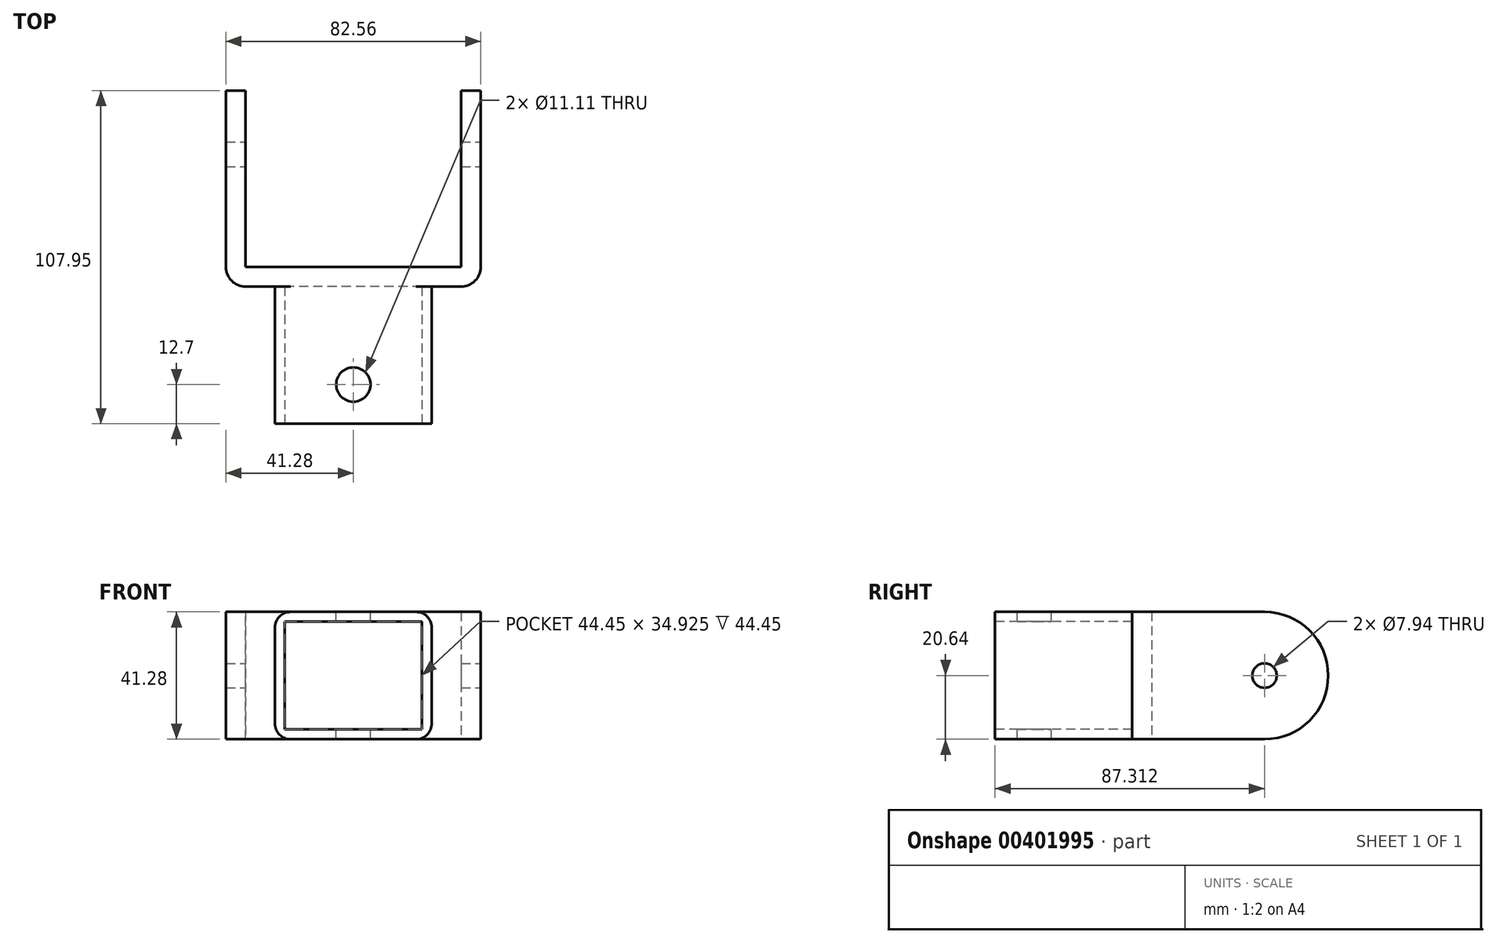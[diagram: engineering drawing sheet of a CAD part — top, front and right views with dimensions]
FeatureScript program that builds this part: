
annotation { "Feature Type Name" : "Feature", "Feature Type Description" : "" }
export const myFeature = defineFeature(function(context is Context, id is Id, definition is map)
    precondition{}
    {
        {
            var Q0;
            Q0=qCreatedBy(makeId("Front.planeOp"),FACE);
            var sketch = newSketch(context, id + "F0", { "sketchPlane" : qUnion([Q0])});
            skLineSegment(sketch, "E0.bottom", {"start": v(25.4, 20.64) * mm, "end": v(-25.4, 20.64) * mm});
            skLineSegment(sketch, "E0.top", {"start": v(25.4, -20.64) * mm, "end": v(-25.4, -20.64) * mm});
            skLineSegment(sketch, "E0.left", {"start": v(25.4, 20.64) * mm, "end": v(25.4, -20.64) * mm});
            skLineSegment(sketch, "E0.right", {"start": v(-25.4, 20.64) * mm, "end": v(-25.4, -20.64) * mm});
            skPoint(sketch, "E0.middle", {"position": v(0, 0) * mm});
            skLineSegment(sketch, "E1.bottom", {"start": v(22.23, 17.46) * mm, "end": v(-22.23, 17.46) * mm});
            skLineSegment(sketch, "E1.top", {"start": v(22.23, -17.46) * mm, "end": v(-22.23, -17.46) * mm});
            skLineSegment(sketch, "E1.left", {"start": v(22.23, 17.46) * mm, "end": v(22.23, -17.46) * mm});
            skLineSegment(sketch, "E1.right", {"start": v(-22.23, 17.46) * mm, "end": v(-22.23, -17.46) * mm});
            skSolve(sketch);
        }
        {
            var Q0;
            Q0=makeQuery(id+"F0.imprint","IMPRINT",FACE,{"disambiguationData":[TD([[makeQuery(id+"F0.imprint","IMPRINT",EDGE,{"derivedFrom":sQuery(id+"F0.wireOp",EDGE,"E0.bottom")}),1.0]])]});
            extrude(context, id + "F1", {"entities" : qUnion([Q0]), "oppositeDirection" : true, "depth" : 44.45 * mm});
        }
        {
            var Q0;
            Q0=qCreatedBy(makeId("Top.planeOp"),FACE);
            var sketch = newSketch(context, id + "F2", { "sketchPlane" : qUnion([Q0])});
            skLineSegment(sketch, "E2.bottom", {"start": v(41.27, 107.95) * mm, "end": v(34.93, 107.95) * mm});
            skLineSegment(sketch, "E2.top", {"start": v(41.28, 44.45) * mm, "end": v(-41.28, 44.45) * mm});
            skLineSegment(sketch, "E2.left", {"start": v(41.27, 107.95) * mm, "end": v(41.28, 44.45) * mm});
            skLineSegment(sketch, "E2.right", {"start": v(-41.28, 107.95) * mm, "end": v(-41.27, 44.45) * mm});
            skPoint(sketch, "E2.middle", {"position": v(0, 76.2) * mm});
            skLineSegment(sketch, "E3.top", {"start": v(34.93, 50.8) * mm, "end": v(-34.93, 50.8) * mm});
            skLineSegment(sketch, "E3.left", {"start": v(34.93, 101.6) * mm, "end": v(34.93, 50.8) * mm});
            skLineSegment(sketch, "E3.right", {"start": v(-34.93, 101.6) * mm, "end": v(-34.93, 50.8) * mm});
            skLineSegment(sketch, "E4", {"start": v(-34.93, 101.6) * mm, "end": v(-34.93, 107.95) * mm});
            skLineSegment(sketch, "E5", {"start": v(34.93, 101.6) * mm, "end": v(34.93, 107.95) * mm});
            skLineSegment(sketch, "E6.trimOffspring", {"start": v(-34.93, 107.95) * mm, "end": v(-41.28, 107.95) * mm});
            skSolve(sketch);
        }
        {
            var Q0;
            Q0 = qSketchRegion(id + "F2", true);
            extrude(context, id + "F3", {"entities" : qUnion([Q0]), "operationType" : NewBodyOperationType.ADD, "depth" : 41.27 * mm, "symmetric" : true});
        }
        {
            var Q0;
            Q0=makeQuery(id+"F3.opExtrude","SWEPT_FACE",FACE,{"disambiguationData":[OSD([sQuery(id+"F2.wireOp",EDGE,"E2.right")])]});
            var sketch = newSketch(context, id + "F4", { "sketchPlane" : qUnion([Q0])});
            skPoint(sketch, "E7", {"position": v(-87.31, 0) * mm});
            skCircle(sketch, "E8", {"center": v(-87.31, 0) * mm, "radius": 20.64 * mm});
            skSolve(sketch);
        }
        {
            var Q0;
            {var subQ0=sQuery(id+"F4.wireOp",EDGE,"E8");var subQ1=sQuery(id+"F2.wireOp",EDGE,"E2.right");var subQ4=makeQuery(id+"F3.opExtrude","CAP_EDGE",EDGE,{"disambiguationData":[OSD([subQ1])],"isStart":true});var subQ5=makeQuery(id+"F4.imprint","INTERSECT",VERTEX,{"derivedFrom":[subQ4,subQ0]});Q0=makeQuery(id+"F4.imprint","IMPRINT",FACE,{"disambiguationData":[TD([[makeQuery(id+"F4.imprint","IMPRINT",EDGE,{"disambiguationData":[TD([[subQ5,1.0]])],"derivedFrom":subQ0}),-1.0]])]});}
            var Q1;
            {var subQ0=sQuery(id+"F4.wireOp",EDGE,"E8");var subQ1=sQuery(id+"F2.wireOp",EDGE,"E2.right");var subQ4=makeQuery(id+"F3.opExtrude","CAP_EDGE",EDGE,{"disambiguationData":[OSD([subQ1])],"isStart":false});var subQ5=makeQuery(id+"F4.imprint","INTERSECT",VERTEX,{"derivedFrom":[subQ4,subQ0]});Q1=makeQuery(id+"F4.imprint","IMPRINT",FACE,{"disambiguationData":[TD([[makeQuery(id+"F4.imprint","IMPRINT",EDGE,{"disambiguationData":[TD([[subQ5,-1.0]])],"derivedFrom":subQ0}),-1.0]])]});}
            extrude(context, id + "F5", {"entities" : qUnion([Q0, Q1]), "operationType" : NewBodyOperationType.REMOVE, "endBound" : BoundingType.THROUGH_ALL, "oppositeDirection" : true, "depth" : 25.4 * mm});
        }
        {
            var Q0;
            Q0=makeQuery(id+"F3.opExtrude","SWEPT_FACE",FACE,{"disambiguationData":[OSD([sQuery(id+"F2.wireOp",EDGE,"E2.right")])]});
            var sketch = newSketch(context, id + "F6", { "sketchPlane" : qUnion([Q0])});
            skPoint(sketch, "E9", {"position": v(-87.31, 0) * mm});
            skSolve(sketch);
        }
        {
            var Q0;
            Q0=sQuery(id+"F6.wireOp",VERTEX,"E9");
            var Q1;
            Q1=makeQuery(id+"F1.opExtrude","SWEPT_BODY",BODY,{"disambiguationData":[OSD([sQuery(id+"F0.wireOp",EDGE,"E0.bottom"),sQuery(id+"F0.wireOp",EDGE,"E0.top"),sQuery(id+"F0.wireOp",EDGE,"E0.left"),sQuery(id+"F0.wireOp",EDGE,"E0.right"),sQuery(id+"F0.wireOp",EDGE,"E1.bottom"),sQuery(id+"F0.wireOp",EDGE,"E1.top"),sQuery(id+"F0.wireOp",EDGE,"E1.left"),sQuery(id+"F0.wireOp",EDGE,"E1.right")])]});
            hole(context, id + "F7", {"style" : HoleStyle.SIMPLE, "endStyle" : HoleEndStyle.THROUGH, "holeDiameter" : 7.94 * mm, "isTappedThrough" : true, "tappedDepth" : 12.7 * mm, "tapClearance" : 3, "locations" : qUnion([Q0]), "scope" : qUnion([Q1])});
        }
        {
            var Q0;
            Q0=makeQuery(id+"F3.opExtrude","SWEPT_EDGE",EDGE,{"disambiguationData":[OSD([sQuery(id+"F2.wireOp",EDGE,"E2.top"),sQuery(id+"F2.wireOp",EDGE,"E2.right")])]});
            var Q1;
            Q1=makeQuery(id+"F3.opExtrude","SWEPT_EDGE",EDGE,{"disambiguationData":[OSD([sQuery(id+"F2.wireOp",EDGE,"E2.top"),sQuery(id+"F2.wireOp",EDGE,"E2.left")])]});
            fillet(context, id + "F8", {"entities" : qUnion([Q0, Q1]), "radius" : 6.35 * mm, "tangentPropagation" : true, "allowEdgeOverflow" : false});
        }
        {
            var Q0;
            Q0=makeQuery(id+"F1.opExtrude","SWEPT_EDGE",EDGE,{"disambiguationData":[OSD([sQuery(id+"F0.wireOp",EDGE,"E0.bottom"),sQuery(id+"F0.wireOp",EDGE,"E0.right")])]});
            var Q1;
            Q1=makeQuery(id+"F1.opExtrude","SWEPT_EDGE",EDGE,{"disambiguationData":[OSD([sQuery(id+"F0.wireOp",EDGE,"E0.bottom"),sQuery(id+"F0.wireOp",EDGE,"E0.left")])]});
            var Q2;
            Q2=makeQuery(id+"F1.opExtrude","SWEPT_EDGE",EDGE,{"disambiguationData":[OSD([sQuery(id+"F0.wireOp",EDGE,"E0.top"),sQuery(id+"F0.wireOp",EDGE,"E0.left")])]});
            var Q3;
            Q3=makeQuery(id+"F1.opExtrude","SWEPT_EDGE",EDGE,{"disambiguationData":[OSD([sQuery(id+"F0.wireOp",EDGE,"E0.top"),sQuery(id+"F0.wireOp",EDGE,"E0.right")])]});
            fillet(context, id + "F9", {"entities" : qUnion([Q0, Q1, Q2, Q3]), "radius" : 5.08 * mm, "tangentPropagation" : true, "allowEdgeOverflow" : false});
        }
        {
            var Q0;
            Q0=makeQuery(id+"F3.boolean.opBoolean","MERGE",FACE,{"derivedFrom":[makeQuery(id+"F1.opExtrude","SWEPT_FACE",FACE,{"disambiguationData":[OSD([sQuery(id+"F0.wireOp",EDGE,"E0.top")])]}),makeQuery(id+"F3.opExtrude","CAP_FACE",FACE,{"disambiguationData":[OSD([sQuery(id+"F2.wireOp",EDGE,"E2.bottom"),sQuery(id+"F2.wireOp",EDGE,"E2.top"),sQuery(id+"F2.wireOp",EDGE,"E2.left"),sQuery(id+"F2.wireOp",EDGE,"E2.right"),sQuery(id+"F2.wireOp",EDGE,"E3.top"),sQuery(id+"F2.wireOp",EDGE,"E3.left"),sQuery(id+"F2.wireOp",EDGE,"E3.right"),sQuery(id+"F2.wireOp",EDGE,"E4"),sQuery(id+"F2.wireOp",EDGE,"E5"),sQuery(id+"F2.wireOp",EDGE,"E6.trimOffspring")])],"isStart":true})]});
            var sketch = newSketch(context, id + "F10", { "sketchPlane" : qUnion([Q0])});
            skPoint(sketch, "E10", {"position": v(0, -12.7) * mm});
            skSolve(sketch);
        }
        {
            var Q0;
            Q0=sQuery(id+"F10.wireOp",VERTEX,"E10");
            var Q1;
            Q1=makeQuery(id+"F1.opExtrude","SWEPT_BODY",BODY,{"disambiguationData":[OSD([sQuery(id+"F0.wireOp",EDGE,"E0.bottom"),sQuery(id+"F0.wireOp",EDGE,"E0.top"),sQuery(id+"F0.wireOp",EDGE,"E0.left"),sQuery(id+"F0.wireOp",EDGE,"E0.right"),sQuery(id+"F0.wireOp",EDGE,"E1.bottom"),sQuery(id+"F0.wireOp",EDGE,"E1.top"),sQuery(id+"F0.wireOp",EDGE,"E1.left"),sQuery(id+"F0.wireOp",EDGE,"E1.right")])]});
            hole(context, id + "F11", {"style" : HoleStyle.SIMPLE, "endStyle" : HoleEndStyle.THROUGH, "holeDiameter" : 11.1 * mm, "isTappedThrough" : true, "tappedDepth" : 12.7 * mm, "tapClearance" : 3, "locations" : qUnion([Q0]), "scope" : qUnion([Q1])});
        }
    });
